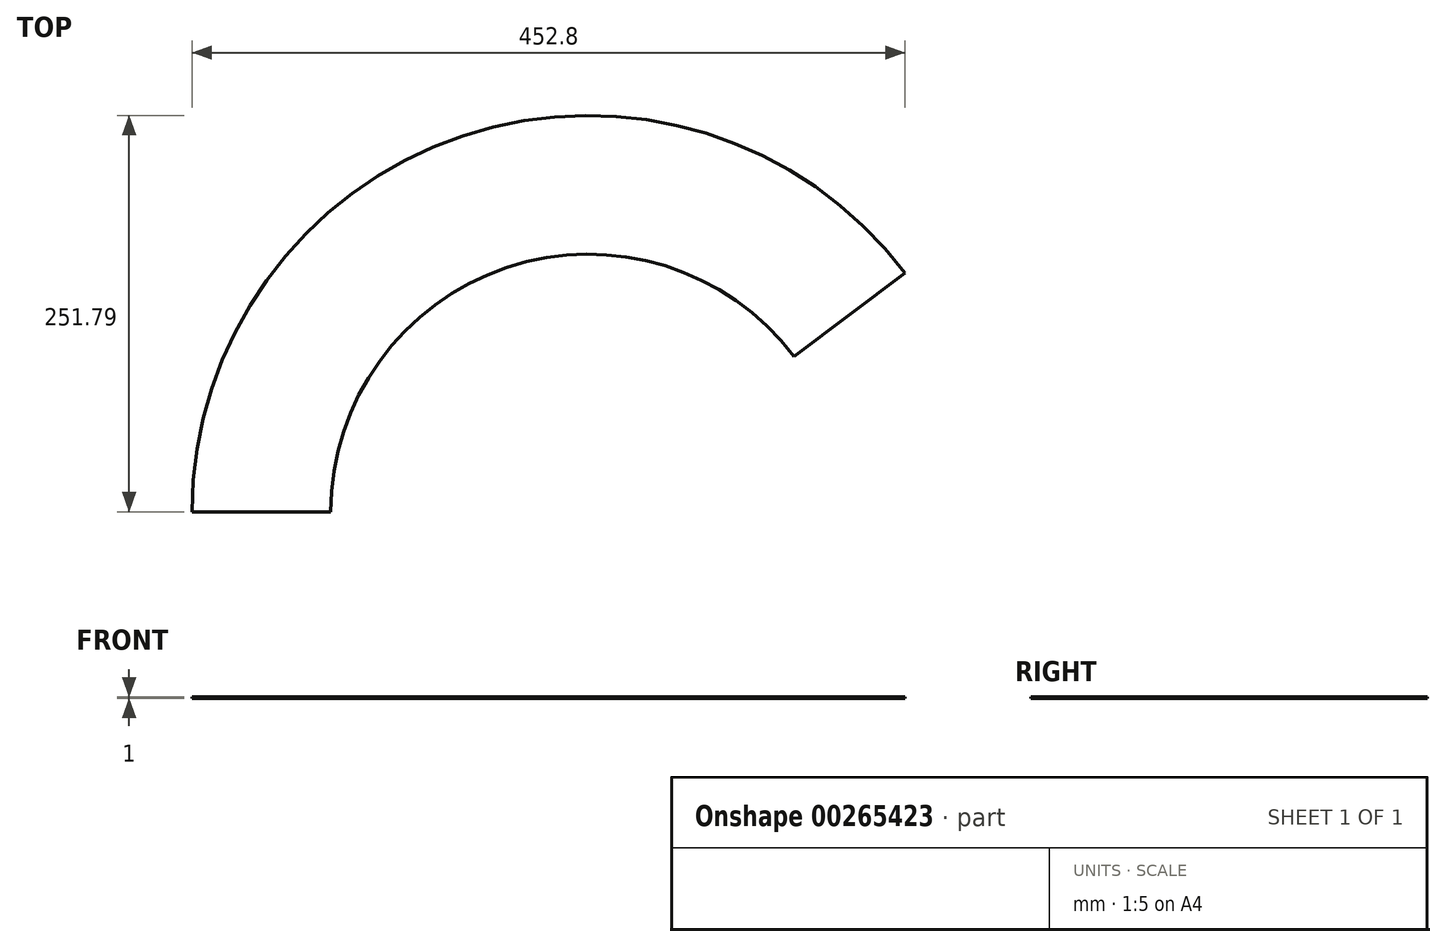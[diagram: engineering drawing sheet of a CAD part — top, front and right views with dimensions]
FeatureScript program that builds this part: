
annotation { "Feature Type Name" : "Feature", "Feature Type Description" : "" }
export const myFeature = defineFeature(function(context is Context, id is Id, definition is map)
    precondition{}
    {
        {
            var Q0;
            Q0=qCreatedBy(makeId("Top.planeOp"),FACE);
            var sketch = newSketch(context, id + "F0", { "sketchPlane" : qUnion([Q0])});
            skCircle(sketch, "E0", {"center": v(0, 0) * mm, "radius": 251.8 * mm});
            skCircle(sketch, "E1", {"center": v(0, 0) * mm, "radius": 163.67 * mm});
            skLineSegment(sketch, "E2", {"start": v(0, 0) * mm, "end": v(-251.8, 0) * mm});
            skLineSegment(sketch, "E3", {"start": v(0, 0) * mm, "end": v(201, 151.64) * mm});
            skSolve(sketch);
        }
        {
            var Q0;
            {var subQ0=sQuery(id+"F0.wireOp",EDGE,"E2");var subQ1=sQuery(id+"F0.wireOp",EDGE,"E0");var subQ2=makeQuery(id+"F0.imprint","INTERSECT",VERTEX,{"derivedFrom":[subQ1,subQ0]});Q0=makeQuery(id+"F0.imprint","IMPRINT",FACE,{"disambiguationData":[TD([[makeQuery(id+"F0.imprint","IMPRINT",EDGE,{"disambiguationData":[TD([[subQ2,1.0]])],"derivedFrom":subQ1}),1.0]])]});}
            extrude(context, id + "F1", {"entities" : qUnion([Q0]), "depth" : 1 * mm});
        }
    });
